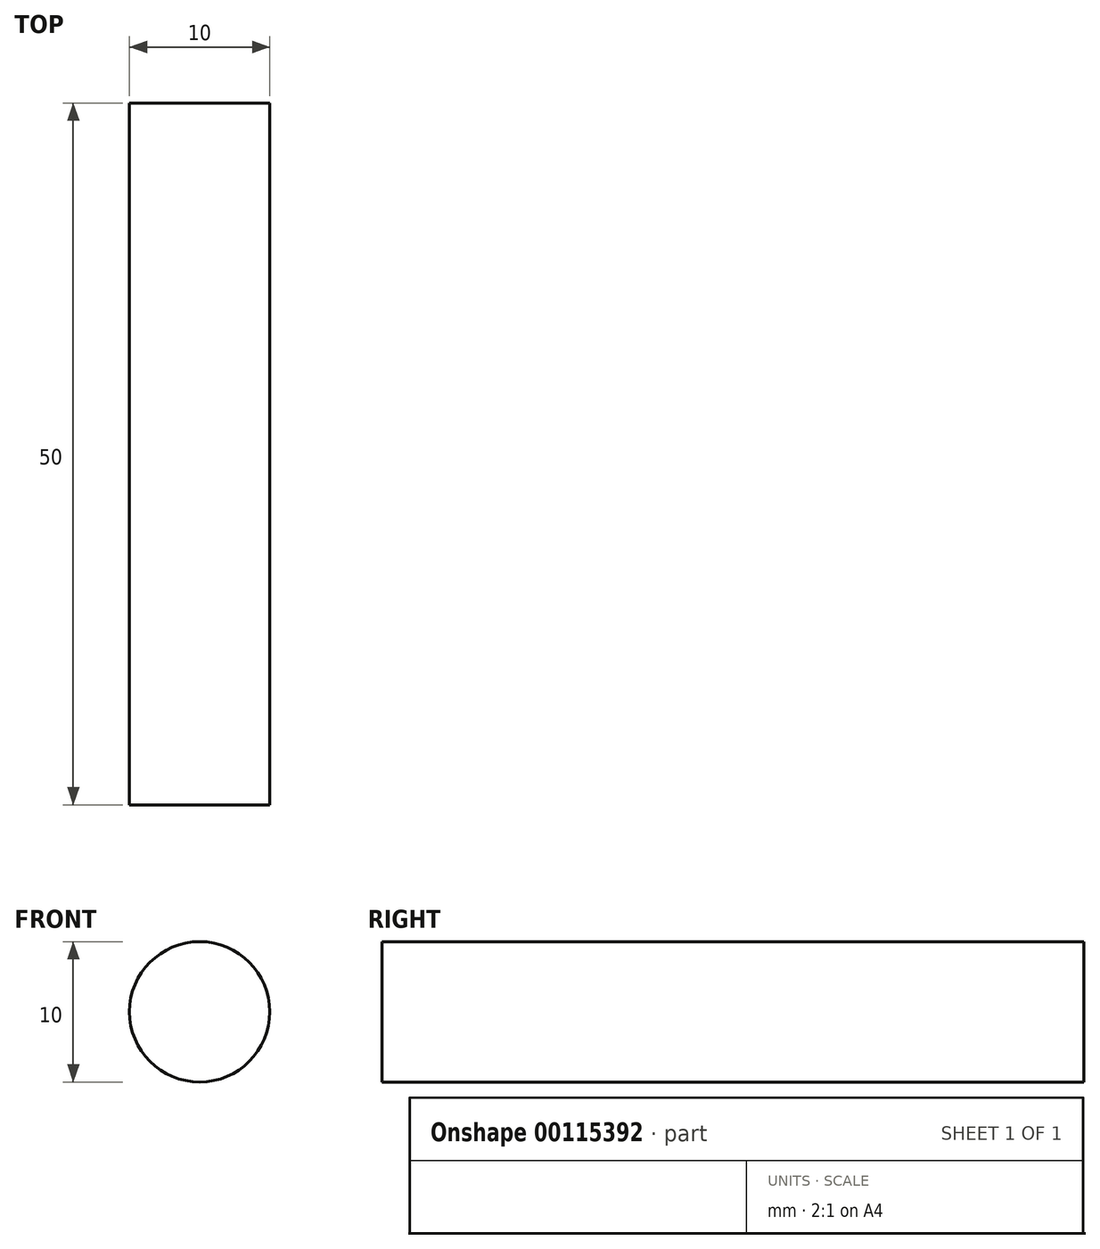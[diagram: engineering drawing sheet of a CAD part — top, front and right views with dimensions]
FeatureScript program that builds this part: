
annotation { "Feature Type Name" : "Feature", "Feature Type Description" : "" }
export const myFeature = defineFeature(function(context is Context, id is Id, definition is map)
    precondition{}
    {
        {
            var Q0;
            Q0=qCreatedBy(makeId("Front.planeOp"),FACE);
            var sketch = newSketch(context, id + "F0", { "sketchPlane" : qUnion([Q0])});
            skCircle(sketch, "E0", {"center": v(0, 0) * mm, "radius": 5 * mm});
            skSolve(sketch);
        }
        {
            var Q0;
            Q0 = qSketchRegion(id + "F0", true);
            extrude(context, id + "F1", {"entities" : qUnion([Q0]), "endBound" : BoundingType.SYMMETRIC, "depth" : 50 * mm});
        }
    });
